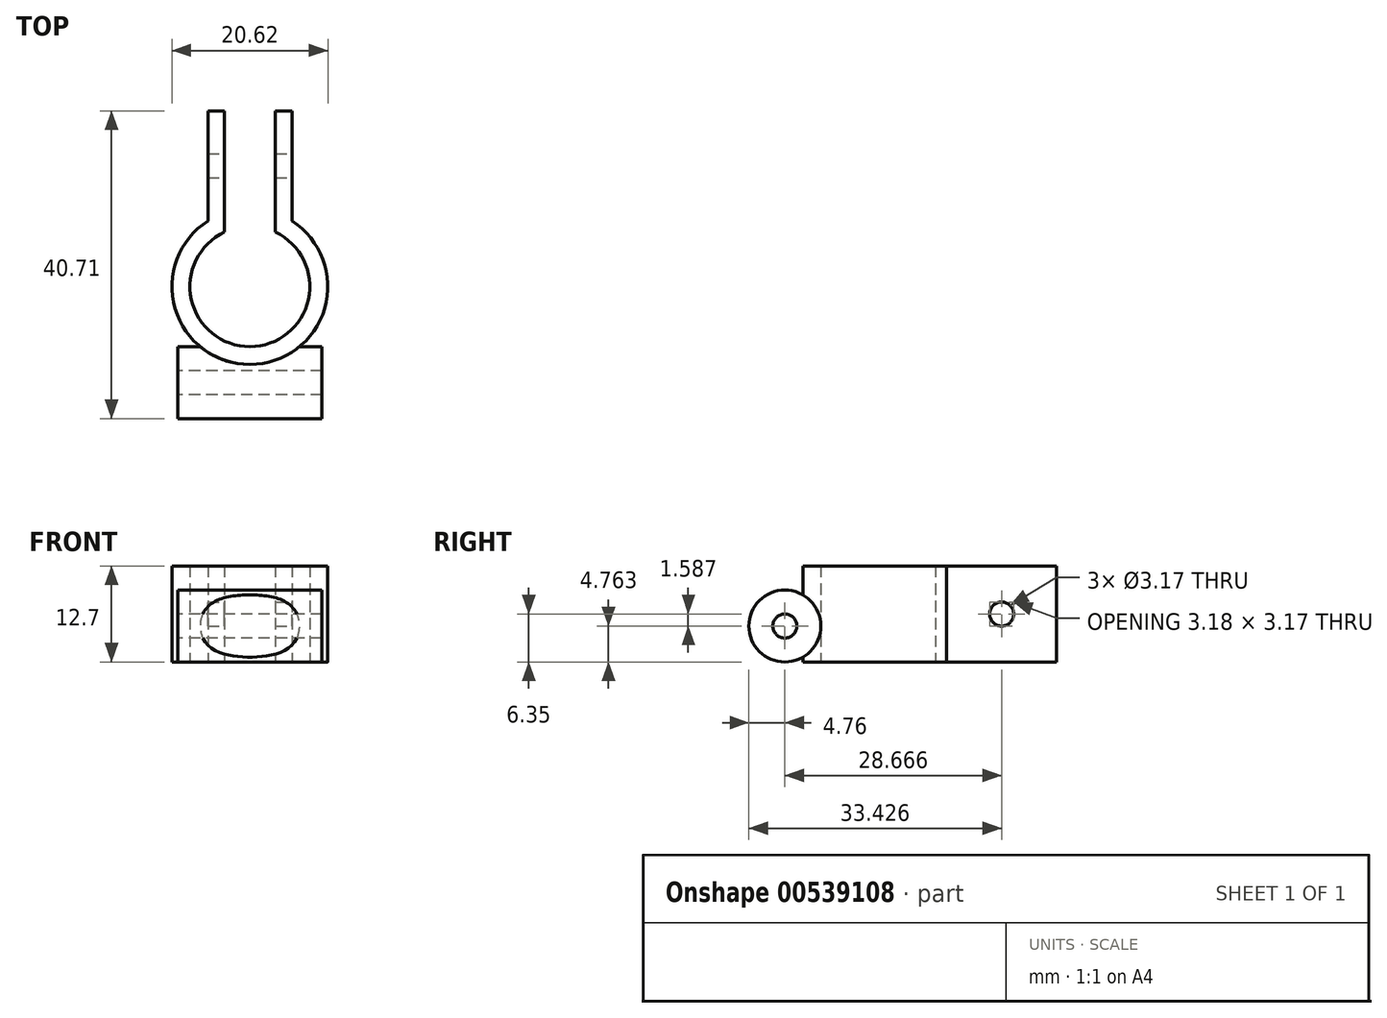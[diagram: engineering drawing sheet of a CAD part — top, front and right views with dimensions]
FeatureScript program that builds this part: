
annotation { "Feature Type Name" : "Feature", "Feature Type Description" : "" }
export const myFeature = defineFeature(function(context is Context, id is Id, definition is map)
    precondition{}
    {
        {
            var Q0;
            Q0=qCreatedBy(makeId("Top.planeOp"),FACE);
            var sketch = newSketch(context, id + "F0", { "sketchPlane" : qUnion([Q0])});
            skArc(sketch, "E0", {"start": v(-5.55, 8.68) * mm, "mid": v(0, -10.3) * mm, "end": v(5.55, 8.68) * mm});
            skLineSegment(sketch, "E1", {"start": v(0, 0) * mm, "end": v(0, 18.27) * mm});
            skLineSegment(sketch, "E2", {"start": v(-5.55, 8.68) * mm, "end": v(-5.55, 5.67) * mm});
            skLineSegment(sketch, "E3.MirrorCS", {"start": v(5.55, 8.68) * mm, "end": v(5.55, 5.67) * mm});
            skLineSegment(sketch, "E4.top", {"start": v(-5.55, 23.25) * mm, "end": v(-3.36, 23.25) * mm});
            skLineSegment(sketch, "E4.left", {"start": v(-5.55, 5.67) * mm, "end": v(-5.55, 23.25) * mm});
            skLineSegment(sketch, "E4.right", {"start": v(-3.36, 7.2) * mm, "end": v(-3.36, 23.25) * mm});
            skArc(sketch, "E5", {"start": v(-3.36, 7.2) * mm, "mid": v(-4.52, 6.52) * mm, "end": v(-5.55, 5.67) * mm});
            skCircle(sketch, "E6", {"center": v(0, 0) * mm, "radius": 7.94 * mm});
            skLineSegment(sketch, "E7.MirrorCS", {"start": v(5.55, 23.25) * mm, "end": v(3.36, 23.25) * mm});
            skLineSegment(sketch, "E8.MirrorCS", {"start": v(3.36, 7.2) * mm, "end": v(3.36, 23.25) * mm});
            skLineSegment(sketch, "E9.MirrorCS", {"start": v(5.55, 5.67) * mm, "end": v(5.55, 23.25) * mm});
            skSolve(sketch);
        }
        {
            var Q0;
            Q0=qCreatedBy(makeId("Right.planeOp"),FACE);
            var sketch = newSketch(context, id + "F1", { "sketchPlane" : qUnion([Q0])});
            skCircle(sketch, "E10", {"center": v(-12.7, 4.76) * mm, "radius": 4.76 * mm});
            skCircle(sketch, "E11", {"center": v(-12.7, 4.76) * mm, "radius": 1.59 * mm});
            skSolve(sketch);
        }
        {
            var Q0;
            {var subQ0=sQuery(id+"F0.wireOp",EDGE,"E0");Q0=makeQuery(id+"F0.imprint","IMPRINT",FACE,{"disambiguationData":[TD([[makeQuery(id+"F0.imprint","IMPRINT",EDGE,{"derivedFrom":subQ0}),1.0]])]});}
            var Q1;
            {var subQ3=sQuery(id+"F0.wireOp",EDGE,"E4.top");Q1=makeQuery(id+"F0.imprint","IMPRINT",FACE,{"disambiguationData":[TD([[makeQuery(id+"F0.imprint","IMPRINT",EDGE,{"derivedFrom":subQ3}),-1.0]])]});}
            var Q2;
            {var subQ4=sQuery(id+"F0.wireOp",EDGE,"E7.MirrorCS");Q2=makeQuery(id+"F0.imprint","IMPRINT",FACE,{"disambiguationData":[TD([[makeQuery(id+"F0.imprint","IMPRINT",EDGE,{"derivedFrom":subQ4}),1.0]])]});}
            extrude(context, id + "F2", {"entities" : qUnion([Q0, Q1, Q2]), "depth" : 12.7 * mm, "offsetDistance" : 25.4 * mm});
        }
        {
            var Q0;
            Q0=makeQuery(id+"F1.imprint","IMPRINT",FACE,{"disambiguationData":[TD([[makeQuery(id+"F1.imprint","IMPRINT",EDGE,{"derivedFrom":sQuery(id+"F1.wireOp",EDGE,"E10")}),1.0]])]});
            extrude(context, id + "F3", {"entities" : qUnion([Q0]), "operationType" : NewBodyOperationType.ADD, "endBound" : BoundingType.SYMMETRIC, "depth" : 19.05 * mm, "offsetDistance" : 25.4 * mm});
        }
        {
            var Q0;
            Q0=makeQuery(id+"F2.opExtrude","SWEPT_FACE",FACE,{"disambiguationData":[OSD([sQuery(id+"F0.wireOp",EDGE,"E9.MirrorCS")])]});
            var sketch = newSketch(context, id + "F4", { "sketchPlane" : qUnion([Q0])});
            skCircle(sketch, "E12", {"center": v(15.97, 6.35) * mm, "radius": 1.59 * mm});
            skSolve(sketch);
        }
        {
            var Q0;
            Q0=makeQuery(id+"F4.imprint","IMPRINT",FACE,{"disambiguationData":[TD([[makeQuery(id+"F4.imprint","IMPRINT",EDGE,{"derivedFrom":sQuery(id+"F4.wireOp",EDGE,"E12")}),1.0]])]});
            extrude(context, id + "F5", {"entities" : qUnion([Q0]), "operationType" : NewBodyOperationType.REMOVE, "endBound" : BoundingType.THROUGH_ALL, "oppositeDirection" : true, "depth" : 25.4 * mm, "offsetDistance" : 25.4 * mm});
        }
        {
            var Q0;
            Q0=makeQuery(id+"F2.opExtrude","SWEPT_BODY",BODY,{"disambiguationData":[OSD([sQuery(id+"F0.wireOp",EDGE,"E0"),sQuery(id+"F0.wireOp",EDGE,"E4.top"),sQuery(id+"F0.wireOp",EDGE,"E4.left"),sQuery(id+"F0.wireOp",EDGE,"E4.right"),sQuery(id+"F0.wireOp",EDGE,"E6"),sQuery(id+"F0.wireOp",EDGE,"E7.MirrorCS"),sQuery(id+"F0.wireOp",EDGE,"E8.MirrorCS"),sQuery(id+"F0.wireOp",EDGE,"E9.MirrorCS")])]});
            transform(context, id + "F6", {"entities" : qUnion([Q0]), "transformType" : TransformType.TRANSLATION_3D, "dx" : 0 * mm, "dy" : 0 * mm, "dz" : 0 * mm, "makeCopy" : true});
        }
        {
            var Q0;
            Q0=makeQuery(id+"F6.opPattern","COPY",BODY,{"derivedFrom":makeQuery(id+"F2.opExtrude","SWEPT_BODY",BODY,{"disambiguationData":[OSD([sQuery(id+"F0.wireOp",EDGE,"E0"),sQuery(id+"F0.wireOp",EDGE,"E4.top"),sQuery(id+"F0.wireOp",EDGE,"E4.left"),sQuery(id+"F0.wireOp",EDGE,"E4.right"),sQuery(id+"F0.wireOp",EDGE,"E6"),sQuery(id+"F0.wireOp",EDGE,"E7.MirrorCS"),sQuery(id+"F0.wireOp",EDGE,"E8.MirrorCS"),sQuery(id+"F0.wireOp",EDGE,"E9.MirrorCS")])]}),"instanceName":"1"});
            deleteBodies(context, id + "F7", {"entities" : qUnion([Q0])});
        }
    });
